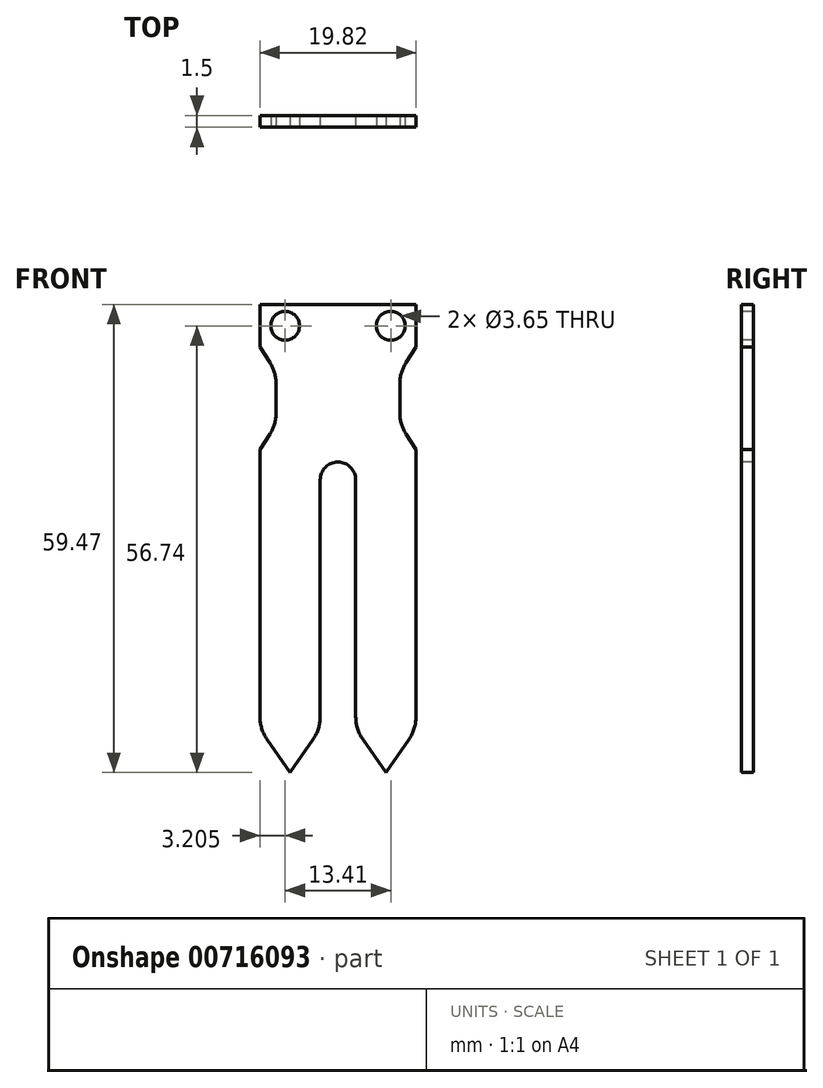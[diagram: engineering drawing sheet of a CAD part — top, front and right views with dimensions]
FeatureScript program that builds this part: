
annotation { "Feature Type Name" : "Feature", "Feature Type Description" : "" }
export const myFeature = defineFeature(function(context is Context, id is Id, definition is map)
    precondition{}
    {
        {
            var Q0;
            Q0=qCreatedBy(makeId("Front.planeOp"),FACE);
            var sketch = newSketch(context, id + "F0", { "sketchPlane" : qUnion([Q0])});
            skLineSegment(sketch, "E0", {"start": v(0, 0) * mm, "end": v(9.9, 0) * mm});
            skLineSegment(sketch, "E1", {"start": v(0, 0) * mm, "end": v(-9.9, 0) * mm});
            skPoint(sketch, "E1.endSnap0", {"position": v(4.96, 0) * mm});
            skLineSegment(sketch, "E2", {"start": v(-9.9, 0) * mm, "end": v(-9.9, -5.46) * mm});
            skLineSegment(sketch, "E3", {"start": v(9.9, 0) * mm, "end": v(9.9, -5.46) * mm});
            skLineSegment(sketch, "E4", {"start": v(9.9, -5.46) * mm, "end": v(7.86, -8.66) * mm});
            skLineSegment(sketch, "E5", {"start": v(-9.91, -5.46) * mm, "end": v(-7.86, -8.66) * mm});
            skLineSegment(sketch, "E6", {"start": v(-7.86, -8.66) * mm, "end": v(-7.86, -15.26) * mm});
            skLineSegment(sketch, "E7", {"start": v(7.86, -8.66) * mm, "end": v(7.86, -15.26) * mm});
            skLineSegment(sketch, "E8", {"start": v(-7.86, -15.26) * mm, "end": v(-9.9, -18.46) * mm});
            skLineSegment(sketch, "E9", {"start": v(7.86, -15.26) * mm, "end": v(9.91, -18.46) * mm});
            skLineSegment(sketch, "E10", {"start": v(-9.9, -18.46) * mm, "end": v(-9.9, -53.97) * mm});
            skLineSegment(sketch, "E11", {"start": v(9.91, -18.46) * mm, "end": v(9.91, -53.97) * mm});
            skLineSegment(sketch, "E12", {"start": v(-9.9, -53.97) * mm, "end": v(-6.08, -59.47) * mm});
            skLineSegment(sketch, "E13", {"start": v(9.91, -53.97) * mm, "end": v(6.08, -59.47) * mm});
            skLineSegment(sketch, "E14", {"start": v(-6.08, -59.47) * mm, "end": v(-2.26, -53.97) * mm});
            skLineSegment(sketch, "E15", {"start": v(6.08, -59.47) * mm, "end": v(2.26, -53.97) * mm});
            skPoint(sketch, "E16.center.orphan", {"position": v(0, -23.67) * mm});
            skLineSegment(sketch, "E17", {"start": v(2.26, -53.97) * mm, "end": v(2.26, -22.3) * mm});
            skLineSegment(sketch, "E18", {"start": v(-2.26, -53.97) * mm, "end": v(-2.26, -22.3) * mm});
            skArc(sketch, "E19", {"start": v(2.26, -22.3) * mm, "mid": v(0, -20.04) * mm, "end": v(-2.26, -22.3) * mm});
            skCircle(sketch, "E20", {"center": v(-6.7, -2.73) * mm, "radius": 1.82 * mm});
            skPoint(sketch, "E20.centerSnap0", {"position": v(-9.9, -2.73) * mm});
            skCircle(sketch, "E21", {"center": v(6.7, -2.73) * mm, "radius": 1.82 * mm});
            skSolve(sketch);
        }
        {
            var Q0;
            Q0=makeQuery(id+"F0.imprint","IMPRINT",FACE,{"disambiguationData":[TD([[makeQuery(id+"F0.imprint","IMPRINT",EDGE,{"derivedFrom":sQuery(id+"F0.wireOp",EDGE,"E0")}),-1.0]])]});
            extrude(context, id + "F1", {"entities" : qUnion([Q0]), "oppositeDirection" : true, "depth" : 1.5 * mm, "offsetDistance" : 25 * mm});
        }
        {
            var Q0;
            Q0=makeQuery(id+"F1.opExtrude","SWEPT_EDGE",EDGE,{"disambiguationData":[OSD([sQuery(id+"F0.wireOp",EDGE,"E7"),sQuery(id+"F0.wireOp",EDGE,"E9")])]});
            var Q1;
            Q1=makeQuery(id+"F1.opExtrude","SWEPT_EDGE",EDGE,{"disambiguationData":[OSD([sQuery(id+"F0.wireOp",EDGE,"E6"),sQuery(id+"F0.wireOp",EDGE,"E8")])]});
            var Q2;
            Q2=makeQuery(id+"F1.opExtrude","SWEPT_EDGE",EDGE,{"disambiguationData":[OSD([sQuery(id+"F0.wireOp",EDGE,"E5"),sQuery(id+"F0.wireOp",EDGE,"E6")])]});
            var Q3;
            Q3=makeQuery(id+"F1.opExtrude","SWEPT_EDGE",EDGE,{"disambiguationData":[OSD([sQuery(id+"F0.wireOp",EDGE,"E4"),sQuery(id+"F0.wireOp",EDGE,"E7")])]});
            var Q4;
            Q4=makeQuery(id+"F1.opExtrude","SWEPT_EDGE",EDGE,{"disambiguationData":[OSD([sQuery(id+"F0.wireOp",EDGE,"E11"),sQuery(id+"F0.wireOp",EDGE,"E13")])]});
            var Q5;
            Q5=makeQuery(id+"F1.opExtrude","SWEPT_EDGE",EDGE,{"disambiguationData":[OSD([sQuery(id+"F0.wireOp",EDGE,"E15"),sQuery(id+"F0.wireOp",EDGE,"E17")])]});
            var Q6;
            Q6=makeQuery(id+"F1.opExtrude","SWEPT_EDGE",EDGE,{"disambiguationData":[OSD([sQuery(id+"F0.wireOp",EDGE,"E10"),sQuery(id+"F0.wireOp",EDGE,"E12")])]});
            var Q7;
            Q7=makeQuery(id+"F1.opExtrude","SWEPT_EDGE",EDGE,{"disambiguationData":[OSD([sQuery(id+"F0.wireOp",EDGE,"E14"),sQuery(id+"F0.wireOp",EDGE,"E18")])]});
            fillet(context, id + "F2", {"entities" : qUnion([Q0, Q1, Q2, Q3, Q4, Q5, Q6, Q7]), "radius" : 5 * mm, "tangentPropagation" : true, "allowEdgeOverflow" : false});
        }
    });
